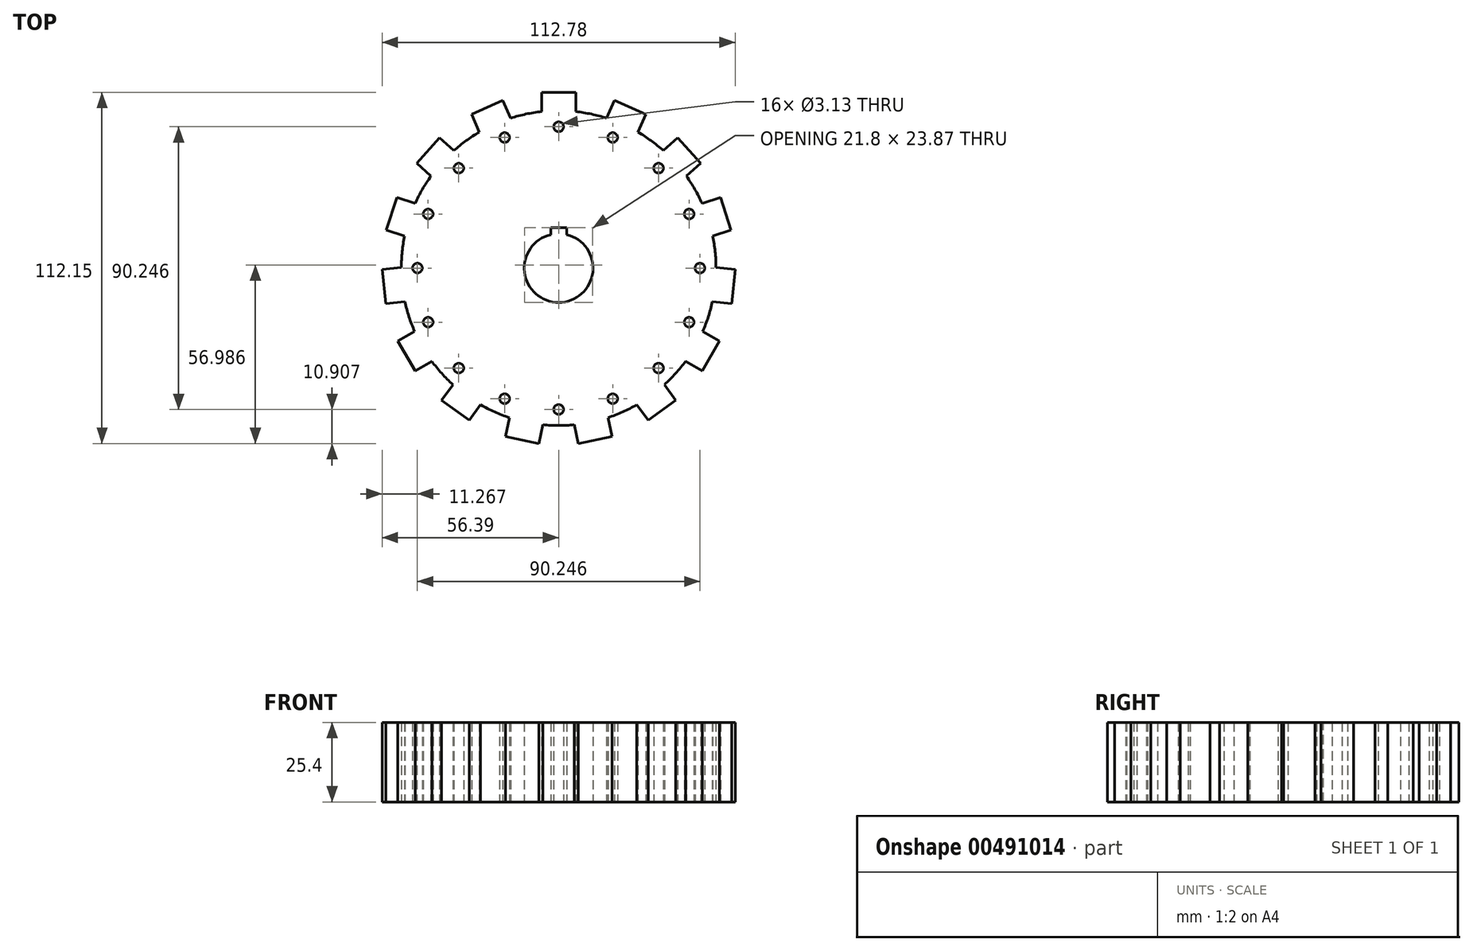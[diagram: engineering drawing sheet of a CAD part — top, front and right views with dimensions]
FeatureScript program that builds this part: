
annotation { "Feature Type Name" : "Feature", "Feature Type Description" : "" }
export const myFeature = defineFeature(function(context is Context, id is Id, definition is map)
    precondition{}
    {
        {
            var Q0;
            Q0=qCreatedBy(makeId("Top.planeOp"),FACE);
            var sketch = newSketch(context, id + "F0", { "sketchPlane" : qUnion([Q0])});
            skCircle(sketch, "E0", {"center": v(0, 0) * mm, "radius": 50.26 * mm});
            skLineSegment(sketch, "E1.bottom", {"start": v(5.47, 56.12) * mm, "end": v(-5.47, 56.12) * mm});
            skLineSegment(sketch, "E1.top", {"start": v(5.47, 44.4) * mm, "end": v(-5.47, 44.4) * mm});
            skLineSegment(sketch, "E1.left", {"start": v(5.47, 56.12) * mm, "end": v(5.47, 44.4) * mm});
            skLineSegment(sketch, "E1.right", {"start": v(-5.47, 56.12) * mm, "end": v(-5.47, 44.4) * mm});
            skPoint(sketch, "E1.middle", {"position": v(0, 50.26) * mm});
            skLineSegment(sketch, "E2.1.0", {"start": v(-27.82, 49.05) * mm, "end": v(-23.06, 38.34) * mm});
            skLineSegment(sketch, "E2.1.1", {"start": v(-17.83, 53.5) * mm, "end": v(-27.82, 49.05) * mm});
            skLineSegment(sketch, "E2.1.2", {"start": v(-17.83, 53.5) * mm, "end": v(-13.07, 42.79) * mm});
            skLineSegment(sketch, "E2.1.3", {"start": v(-13.07, 42.79) * mm, "end": v(-23.06, 38.34) * mm});
            skLineSegment(sketch, "E2.2.0", {"start": v(-45.37, 33.49) * mm, "end": v(-36.66, 25.65) * mm});
            skLineSegment(sketch, "E2.2.1", {"start": v(-38.05, 41.62) * mm, "end": v(-45.37, 33.49) * mm});
            skLineSegment(sketch, "E2.2.2", {"start": v(-38.05, 41.62) * mm, "end": v(-29.34, 33.78) * mm});
            skLineSegment(sketch, "E2.2.3", {"start": v(-29.34, 33.78) * mm, "end": v(-36.66, 25.65) * mm});
            skLineSegment(sketch, "E2.3.0", {"start": v(-55.07, 12.14) * mm, "end": v(-43.92, 8.52) * mm});
            skLineSegment(sketch, "E2.3.1", {"start": v(-51.69, 22.54) * mm, "end": v(-55.07, 12.14) * mm});
            skLineSegment(sketch, "E2.3.2", {"start": v(-51.69, 22.54) * mm, "end": v(-40.54, 18.92) * mm});
            skLineSegment(sketch, "E2.3.3", {"start": v(-40.54, 18.92) * mm, "end": v(-43.92, 8.52) * mm});
            skLineSegment(sketch, "E2.4.0", {"start": v(-55.24, -11.3) * mm, "end": v(-43.59, -10.08) * mm});
            skLineSegment(sketch, "E2.4.1", {"start": v(-56.39, -0.43) * mm, "end": v(-55.24, -11.3) * mm});
            skLineSegment(sketch, "E2.4.2", {"start": v(-56.39, -0.43) * mm, "end": v(-44.73, 0.8) * mm});
            skLineSegment(sketch, "E2.4.3", {"start": v(-44.73, 0.8) * mm, "end": v(-43.59, -10.08) * mm});
            skLineSegment(sketch, "E2.5.0", {"start": v(-45.87, -32.8) * mm, "end": v(-35.72, -26.94) * mm});
            skLineSegment(sketch, "E2.5.1", {"start": v(-51.34, -23.33) * mm, "end": v(-45.87, -32.8) * mm});
            skLineSegment(sketch, "E2.5.2", {"start": v(-51.34, -23.33) * mm, "end": v(-41.19, -17.47) * mm});
            skLineSegment(sketch, "E2.5.3", {"start": v(-41.19, -17.47) * mm, "end": v(-35.72, -26.94) * mm});
            skLineSegment(sketch, "E2.6.0", {"start": v(-28.56, -48.62) * mm, "end": v(-21.68, -39.14) * mm});
            skLineSegment(sketch, "E2.6.1", {"start": v(-37.41, -42.19) * mm, "end": v(-28.56, -48.62) * mm});
            skLineSegment(sketch, "E2.6.2", {"start": v(-37.41, -42.19) * mm, "end": v(-30.52, -32.7) * mm});
            skLineSegment(sketch, "E2.6.3", {"start": v(-30.52, -32.7) * mm, "end": v(-21.68, -39.14) * mm});
            skLineSegment(sketch, "E2.7.0", {"start": v(-6.32, -56.03) * mm, "end": v(-3.88, -44.57) * mm});
            skLineSegment(sketch, "E2.7.1", {"start": v(-17.02, -53.76) * mm, "end": v(-6.32, -56.03) * mm});
            skLineSegment(sketch, "E2.7.2", {"start": v(-17.02, -53.76) * mm, "end": v(-14.58, -42.3) * mm});
            skLineSegment(sketch, "E2.7.3", {"start": v(-14.58, -42.3) * mm, "end": v(-3.88, -44.57) * mm});
            skLineSegment(sketch, "E2.8.0", {"start": v(17.02, -53.76) * mm, "end": v(14.58, -42.3) * mm});
            skLineSegment(sketch, "E2.8.1", {"start": v(6.32, -56.03) * mm, "end": v(17.02, -53.76) * mm});
            skLineSegment(sketch, "E2.8.2", {"start": v(6.32, -56.03) * mm, "end": v(3.88, -44.57) * mm});
            skLineSegment(sketch, "E2.8.3", {"start": v(3.88, -44.57) * mm, "end": v(14.58, -42.3) * mm});
            skLineSegment(sketch, "E2.9.0", {"start": v(37.41, -42.19) * mm, "end": v(30.52, -32.7) * mm});
            skLineSegment(sketch, "E2.9.1", {"start": v(28.56, -48.62) * mm, "end": v(37.41, -42.19) * mm});
            skLineSegment(sketch, "E2.9.2", {"start": v(28.56, -48.62) * mm, "end": v(21.68, -39.14) * mm});
            skLineSegment(sketch, "E2.9.3", {"start": v(21.68, -39.14) * mm, "end": v(30.52, -32.7) * mm});
            skLineSegment(sketch, "E2.10.0", {"start": v(51.34, -23.33) * mm, "end": v(41.19, -17.47) * mm});
            skLineSegment(sketch, "E2.10.1", {"start": v(45.87, -32.8) * mm, "end": v(51.34, -23.33) * mm});
            skLineSegment(sketch, "E2.10.2", {"start": v(45.87, -32.8) * mm, "end": v(35.72, -26.94) * mm});
            skLineSegment(sketch, "E2.10.3", {"start": v(35.72, -26.94) * mm, "end": v(41.19, -17.47) * mm});
            skLineSegment(sketch, "E2.11.0", {"start": v(56.39, -0.43) * mm, "end": v(44.73, 0.8) * mm});
            skLineSegment(sketch, "E2.11.1", {"start": v(55.24, -11.3) * mm, "end": v(56.39, -0.43) * mm});
            skLineSegment(sketch, "E2.11.2", {"start": v(55.24, -11.3) * mm, "end": v(43.59, -10.08) * mm});
            skLineSegment(sketch, "E2.11.3", {"start": v(43.59, -10.08) * mm, "end": v(44.73, 0.8) * mm});
            skLineSegment(sketch, "E2.12.0", {"start": v(51.69, 22.54) * mm, "end": v(40.54, 18.92) * mm});
            skLineSegment(sketch, "E2.12.1", {"start": v(55.07, 12.14) * mm, "end": v(51.69, 22.54) * mm});
            skLineSegment(sketch, "E2.12.2", {"start": v(55.07, 12.14) * mm, "end": v(43.92, 8.52) * mm});
            skLineSegment(sketch, "E2.12.3", {"start": v(43.92, 8.52) * mm, "end": v(40.54, 18.92) * mm});
            skLineSegment(sketch, "E2.13.0", {"start": v(38.05, 41.62) * mm, "end": v(29.34, 33.78) * mm});
            skLineSegment(sketch, "E2.13.1", {"start": v(45.37, 33.49) * mm, "end": v(38.05, 41.62) * mm});
            skLineSegment(sketch, "E2.13.2", {"start": v(45.37, 33.49) * mm, "end": v(36.66, 25.65) * mm});
            skLineSegment(sketch, "E2.13.3", {"start": v(36.66, 25.65) * mm, "end": v(29.34, 33.78) * mm});
            skLineSegment(sketch, "E2.14.0", {"start": v(17.83, 53.5) * mm, "end": v(13.07, 42.79) * mm});
            skLineSegment(sketch, "E2.14.1", {"start": v(27.82, 49.05) * mm, "end": v(17.83, 53.5) * mm});
            skLineSegment(sketch, "E2.14.2", {"start": v(27.82, 49.05) * mm, "end": v(23.06, 38.34) * mm});
            skLineSegment(sketch, "E2.14.3", {"start": v(23.06, 38.34) * mm, "end": v(13.07, 42.79) * mm});
            skSolve(sketch);
        }
        {
            var Q0;
            Q0 = qSketchRegion(id + "F0", true);
            extrude(context, id + "F1", {"entities" : qUnion([Q0]), "depth" : 25.4 * mm});
        }
        {
            var Q0;
            Q0=makeQuery(id+"F1.opExtrude","CAP_FACE",FACE,{"disambiguationData":[OSD([sQuery(id+"F0.wireOp",EDGE,"E0"),sQuery(id+"F0.wireOp",EDGE,"E1.bottom"),sQuery(id+"F0.wireOp",EDGE,"E1.left"),sQuery(id+"F0.wireOp",EDGE,"E1.right"),sQuery(id+"F0.wireOp",EDGE,"E2.1.0"),sQuery(id+"F0.wireOp",EDGE,"E2.1.1"),sQuery(id+"F0.wireOp",EDGE,"E2.1.2"),sQuery(id+"F0.wireOp",EDGE,"E2.2.0"),sQuery(id+"F0.wireOp",EDGE,"E2.2.1"),sQuery(id+"F0.wireOp",EDGE,"E2.2.2"),sQuery(id+"F0.wireOp",EDGE,"E2.3.0"),sQuery(id+"F0.wireOp",EDGE,"E2.3.1"),sQuery(id+"F0.wireOp",EDGE,"E2.3.2"),sQuery(id+"F0.wireOp",EDGE,"E2.4.0"),sQuery(id+"F0.wireOp",EDGE,"E2.4.1"),sQuery(id+"F0.wireOp",EDGE,"E2.4.2"),sQuery(id+"F0.wireOp",EDGE,"E2.5.0"),sQuery(id+"F0.wireOp",EDGE,"E2.5.1"),sQuery(id+"F0.wireOp",EDGE,"E2.5.2"),sQuery(id+"F0.wireOp",EDGE,"E2.6.0"),sQuery(id+"F0.wireOp",EDGE,"E2.6.1"),sQuery(id+"F0.wireOp",EDGE,"E2.6.2"),sQuery(id+"F0.wireOp",EDGE,"E2.7.0"),sQuery(id+"F0.wireOp",EDGE,"E2.7.1"),sQuery(id+"F0.wireOp",EDGE,"E2.7.2"),sQuery(id+"F0.wireOp",EDGE,"E2.8.0"),sQuery(id+"F0.wireOp",EDGE,"E2.8.1"),sQuery(id+"F0.wireOp",EDGE,"E2.8.2"),sQuery(id+"F0.wireOp",EDGE,"E2.9.0"),sQuery(id+"F0.wireOp",EDGE,"E2.9.1"),sQuery(id+"F0.wireOp",EDGE,"E2.9.2"),sQuery(id+"F0.wireOp",EDGE,"E2.10.0"),sQuery(id+"F0.wireOp",EDGE,"E2.10.1"),sQuery(id+"F0.wireOp",EDGE,"E2.10.2"),sQuery(id+"F0.wireOp",EDGE,"E2.11.0"),sQuery(id+"F0.wireOp",EDGE,"E2.11.1"),sQuery(id+"F0.wireOp",EDGE,"E2.11.2"),sQuery(id+"F0.wireOp",EDGE,"E2.12.0"),sQuery(id+"F0.wireOp",EDGE,"E2.12.1"),sQuery(id+"F0.wireOp",EDGE,"E2.12.2"),sQuery(id+"F0.wireOp",EDGE,"E2.13.0"),sQuery(id+"F0.wireOp",EDGE,"E2.13.1"),sQuery(id+"F0.wireOp",EDGE,"E2.13.2"),sQuery(id+"F0.wireOp",EDGE,"E2.14.0"),sQuery(id+"F0.wireOp",EDGE,"E2.14.1"),sQuery(id+"F0.wireOp",EDGE,"E2.14.2")])],"isStart":true});
            var sketch = newSketch(context, id + "F2", { "sketchPlane" : qUnion([Q0])});
            skCircle(sketch, "E3", {"center": v(0, 0) * mm, "radius": 10.98 * mm});
            skSolve(sketch);
        }
        {
            var Q0;
            Q0 = qSketchRegion(id + "F2", true);
            extrude(context, id + "F3", {"entities" : qUnion([Q0]), "operationType" : NewBodyOperationType.REMOVE, "oppositeDirection" : true, "depth" : 49.53 * mm});
        }
        {
            var Q0;
            Q0=makeQuery(id+"F1.opExtrude","CAP_FACE",FACE,{"disambiguationData":[OSD([sQuery(id+"F0.wireOp",EDGE,"E0"),sQuery(id+"F0.wireOp",EDGE,"E1.bottom"),sQuery(id+"F0.wireOp",EDGE,"E1.left"),sQuery(id+"F0.wireOp",EDGE,"E1.right"),sQuery(id+"F0.wireOp",EDGE,"E2.1.0"),sQuery(id+"F0.wireOp",EDGE,"E2.1.1"),sQuery(id+"F0.wireOp",EDGE,"E2.1.2"),sQuery(id+"F0.wireOp",EDGE,"E2.2.0"),sQuery(id+"F0.wireOp",EDGE,"E2.2.1"),sQuery(id+"F0.wireOp",EDGE,"E2.2.2"),sQuery(id+"F0.wireOp",EDGE,"E2.3.0"),sQuery(id+"F0.wireOp",EDGE,"E2.3.1"),sQuery(id+"F0.wireOp",EDGE,"E2.3.2"),sQuery(id+"F0.wireOp",EDGE,"E2.4.0"),sQuery(id+"F0.wireOp",EDGE,"E2.4.1"),sQuery(id+"F0.wireOp",EDGE,"E2.4.2"),sQuery(id+"F0.wireOp",EDGE,"E2.5.0"),sQuery(id+"F0.wireOp",EDGE,"E2.5.1"),sQuery(id+"F0.wireOp",EDGE,"E2.5.2"),sQuery(id+"F0.wireOp",EDGE,"E2.6.0"),sQuery(id+"F0.wireOp",EDGE,"E2.6.1"),sQuery(id+"F0.wireOp",EDGE,"E2.6.2"),sQuery(id+"F0.wireOp",EDGE,"E2.7.0"),sQuery(id+"F0.wireOp",EDGE,"E2.7.1"),sQuery(id+"F0.wireOp",EDGE,"E2.7.2"),sQuery(id+"F0.wireOp",EDGE,"E2.8.0"),sQuery(id+"F0.wireOp",EDGE,"E2.8.1"),sQuery(id+"F0.wireOp",EDGE,"E2.8.2"),sQuery(id+"F0.wireOp",EDGE,"E2.9.0"),sQuery(id+"F0.wireOp",EDGE,"E2.9.1"),sQuery(id+"F0.wireOp",EDGE,"E2.9.2"),sQuery(id+"F0.wireOp",EDGE,"E2.10.0"),sQuery(id+"F0.wireOp",EDGE,"E2.10.1"),sQuery(id+"F0.wireOp",EDGE,"E2.10.2"),sQuery(id+"F0.wireOp",EDGE,"E2.11.0"),sQuery(id+"F0.wireOp",EDGE,"E2.11.1"),sQuery(id+"F0.wireOp",EDGE,"E2.11.2"),sQuery(id+"F0.wireOp",EDGE,"E2.12.0"),sQuery(id+"F0.wireOp",EDGE,"E2.12.1"),sQuery(id+"F0.wireOp",EDGE,"E2.12.2"),sQuery(id+"F0.wireOp",EDGE,"E2.13.0"),sQuery(id+"F0.wireOp",EDGE,"E2.13.1"),sQuery(id+"F0.wireOp",EDGE,"E2.13.2"),sQuery(id+"F0.wireOp",EDGE,"E2.14.0"),sQuery(id+"F0.wireOp",EDGE,"E2.14.1"),sQuery(id+"F0.wireOp",EDGE,"E2.14.2")])],"isStart":false});
            var sketch = newSketch(context, id + "F4", { "sketchPlane" : qUnion([Q0])});
            skLineSegment(sketch, "E4.bottom", {"start": v(2.56, 12.89) * mm, "end": v(-2.56, 12.89) * mm});
            skLineSegment(sketch, "E4.top", {"start": v(2.56, 6.38) * mm, "end": v(-2.56, 6.38) * mm});
            skLineSegment(sketch, "E4.left", {"start": v(2.56, 12.89) * mm, "end": v(2.56, 6.38) * mm});
            skLineSegment(sketch, "E4.right", {"start": v(-2.56, 12.89) * mm, "end": v(-2.56, 6.38) * mm});
            skPoint(sketch, "E4.middle", {"position": v(0, 9.63) * mm});
            skSolve(sketch);
        }
        {
            var Q0;
            Q0 = qSketchRegion(id + "F4", true);
            extrude(context, id + "F5", {"entities" : qUnion([Q0]), "operationType" : NewBodyOperationType.REMOVE, "oppositeDirection" : true, "depth" : 48.5 * mm});
        }
        {
            var Q0;
            Q0=qCreatedBy(makeId("Top.planeOp"),FACE);
            var sketch = newSketch(context, id + "F6", { "sketchPlane" : qUnion([Q0])});
            skCircle(sketch, "E5", {"center": v(0, 45.12) * mm, "radius": 1.56 * mm});
            skCircle(sketch, "E6.1.0", {"center": v(-17.27, 41.69) * mm, "radius": 1.56 * mm});
            skCircle(sketch, "E6.2.0", {"center": v(-31.9, 31.9) * mm, "radius": 1.56 * mm});
            skCircle(sketch, "E6.3.0", {"center": v(-41.69, 17.27) * mm, "radius": 1.56 * mm});
            skCircle(sketch, "E6.4.0", {"center": v(-45.12, 0) * mm, "radius": 1.56 * mm});
            skCircle(sketch, "E6.5.0", {"center": v(-41.69, -17.27) * mm, "radius": 1.56 * mm});
            skCircle(sketch, "E6.6.0", {"center": v(-31.9, -31.9) * mm, "radius": 1.56 * mm});
            skCircle(sketch, "E6.7.0", {"center": v(-17.27, -41.69) * mm, "radius": 1.56 * mm});
            skCircle(sketch, "E6.8.0", {"center": v(0, -45.12) * mm, "radius": 1.56 * mm});
            skCircle(sketch, "E6.9.0", {"center": v(17.27, -41.69) * mm, "radius": 1.56 * mm});
            skCircle(sketch, "E6.10.0", {"center": v(31.9, -31.9) * mm, "radius": 1.56 * mm});
            skCircle(sketch, "E6.11.0", {"center": v(41.69, -17.27) * mm, "radius": 1.56 * mm});
            skCircle(sketch, "E6.12.0", {"center": v(45.12, 0) * mm, "radius": 1.56 * mm});
            skCircle(sketch, "E6.13.0", {"center": v(41.69, 17.27) * mm, "radius": 1.56 * mm});
            skCircle(sketch, "E6.14.0", {"center": v(31.9, 31.9) * mm, "radius": 1.56 * mm});
            skCircle(sketch, "E6.15.0", {"center": v(17.27, 41.69) * mm, "radius": 1.56 * mm});
            skPoint(sketch, "E6.center", {"position": v(0, 0) * mm});
            skSolve(sketch);
        }
        {
            var Q0;
            Q0 = qSketchRegion(id + "F6", true);
            extrude(context, id + "F7", {"entities" : qUnion([Q0]), "operationType" : NewBodyOperationType.REMOVE, "depth" : 173.33 * mm});
        }
    });
